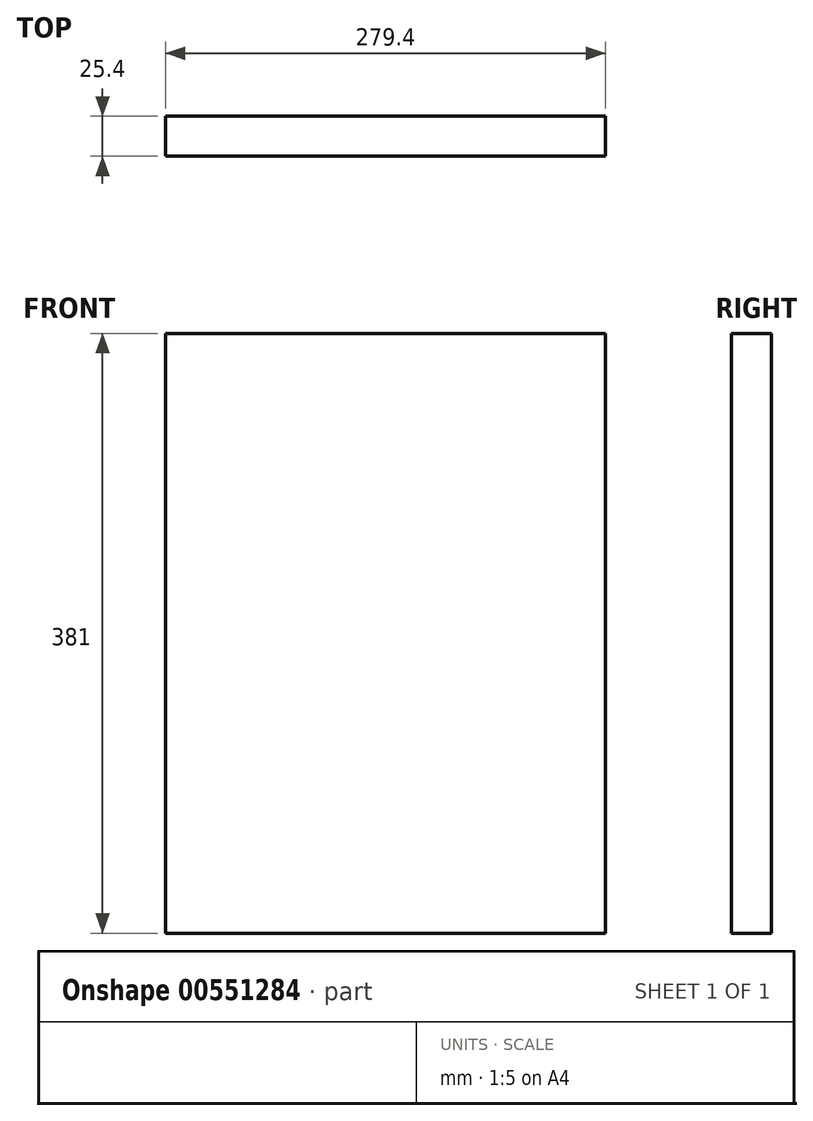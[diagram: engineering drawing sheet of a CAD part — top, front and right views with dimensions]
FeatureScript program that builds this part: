
annotation { "Feature Type Name" : "Feature", "Feature Type Description" : "" }
export const myFeature = defineFeature(function(context is Context, id is Id, definition is map)
    precondition{}
    {
        {
            var Q0;
            Q0=qCreatedBy(makeId("Front.planeOp"),FACE);
            var sketch = newSketch(context, id + "F0", { "sketchPlane" : qUnion([Q0])});
            skLineSegment(sketch, "E0.bottom", {"start": v(228.6, 0) * mm, "end": v(0, 0) * mm});
            skLineSegment(sketch, "E0.top", {"start": v(228.6, -381) * mm, "end": v(0, -381) * mm});
            skLineSegment(sketch, "E0.left", {"start": v(228.6, 0) * mm, "end": v(228.6, -381) * mm});
            skLineSegment(sketch, "E0.right", {"start": v(0, 0) * mm, "end": v(0, -381) * mm});
            skSolve(sketch);
        }
        {
            var Q0;
            Q0=makeQuery(id+"F0.imprint","IMPRINT",FACE,{"disambiguationData":[TD([[makeQuery(id+"F0.imprint","IMPRINT",EDGE,{"derivedFrom":sQuery(id+"F0.wireOp",EDGE,"E0.bottom")}),1.0]])]});
            extrude(context, id + "F1", {"entities" : qUnion([Q0]), "depth" : 25.4 * mm, "offsetDistance" : 25.4 * mm});
        }
        {
            var Q0;
            Q0=makeQuery(id+"F1.opExtrude","SWEPT_FACE",FACE,{"disambiguationData":[OSD([sQuery(id+"F0.wireOp",EDGE,"E0.left")])]});
            extrude(context, id + "F2", {"entities" : qUnion([Q0]), "operationType" : NewBodyOperationType.ADD, "depth" : 50.8 * mm, "offsetDistance" : 25.4 * mm});
        }
    });
